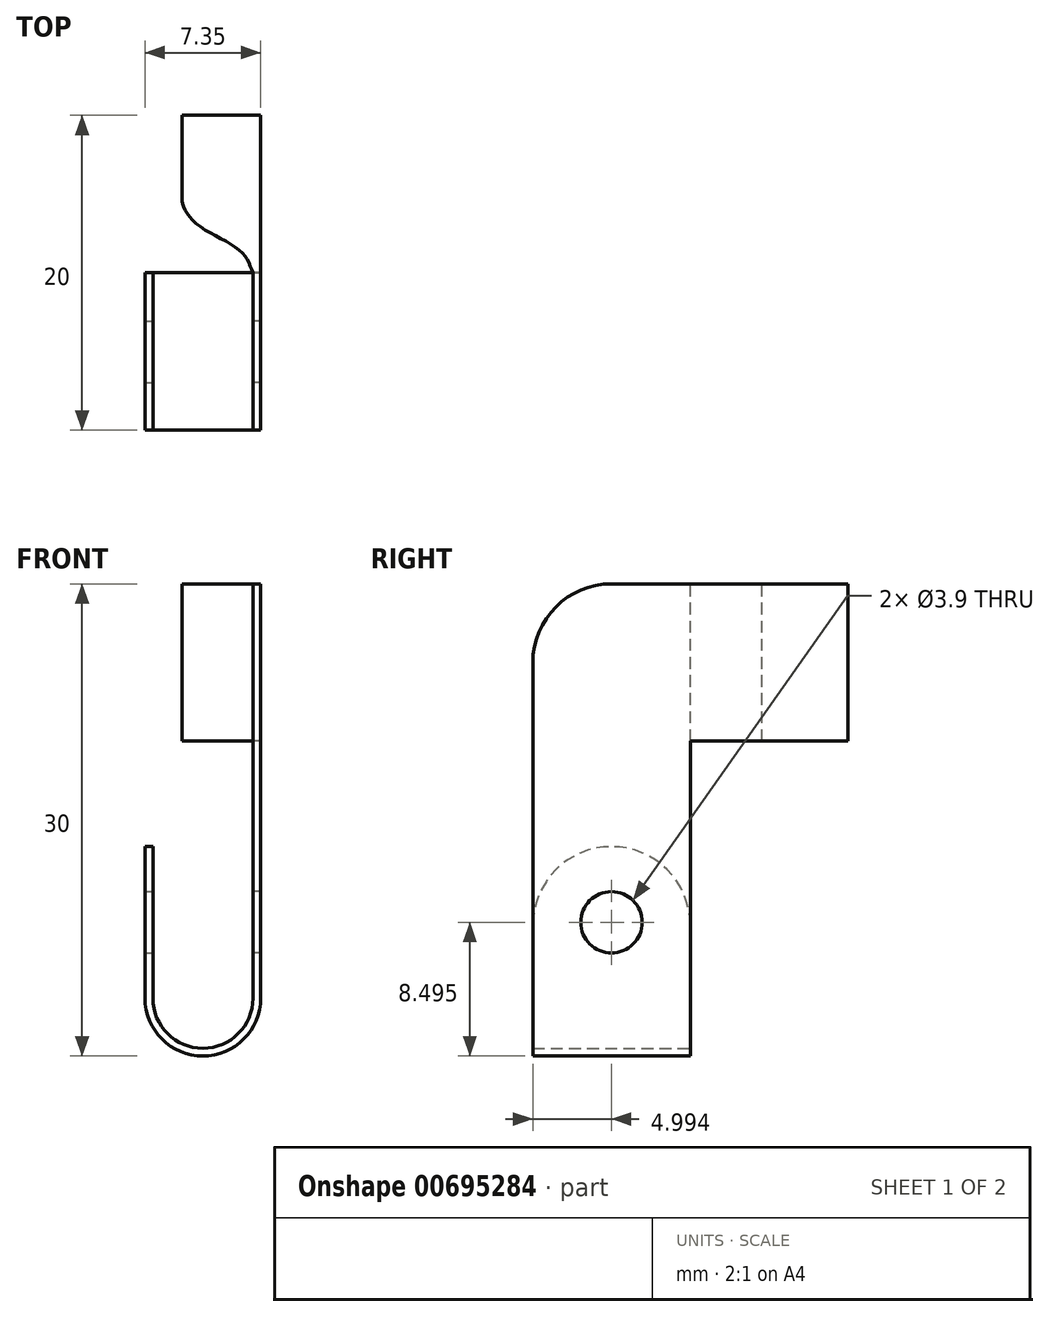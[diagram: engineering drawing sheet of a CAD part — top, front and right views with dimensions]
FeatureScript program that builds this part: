
annotation { "Feature Type Name" : "Feature", "Feature Type Description" : "" }
export const myFeature = defineFeature(function(context is Context, id is Id, definition is map)
    precondition{}
    {
        {
            var Q0;
            Q0=qCreatedBy(makeId("Front.planeOp"),FACE);
            var sketch = newSketch(context, id + "F0", { "sketchPlane" : qUnion([Q0])});
            skLineSegment(sketch, "E0", {"start": v(0, 0) * mm, "end": v(7.44, 0) * mm, "construction": true});
            skLineSegment(sketch, "E1", {"start": v(0, 0) * mm, "end": v(0, 6.37) * mm, "construction": true});
            skArc(sketch, "E2", {"start": v(0, 3.68) * mm, "mid": v(3.67, 0) * mm, "end": v(7.35, 3.67) * mm});
            skArc(sketch, "E3", {"start": v(0.5, 3.68) * mm, "mid": v(3.67, 0.5) * mm, "end": v(6.85, 3.67) * mm});
            skLineSegment(sketch, "E4", {"start": v(0, 3.67) * mm, "end": v(7.35, 3.67) * mm, "construction": true});
            skLineSegment(sketch, "E5", {"start": v(0, 3.68) * mm, "end": v(0, 11.52) * mm});
            skLineSegment(sketch, "E6", {"start": v(0, 15.1) * mm, "end": v(0, 11.52) * mm});
            skLineSegment(sketch, "E7", {"start": v(7.35, 3.67) * mm, "end": v(7.35, 0) * mm, "construction": true});
            skLineSegment(sketch, "E8", {"start": v(6.85, 3.67) * mm, "end": v(6.85, 0) * mm, "construction": true});
            skLineSegment(sketch, "E9", {"start": v(7.35, 3.67) * mm, "end": v(7.35, 20) * mm});
            skLineSegment(sketch, "E10", {"start": v(7.35, 20) * mm, "end": v(6.85, 20) * mm});
            skLineSegment(sketch, "E11", {"start": v(6.85, 20) * mm, "end": v(6.85, 3.67) * mm});
            skLineSegment(sketch, "E12", {"start": v(7.35, 20) * mm, "end": v(7.35, 30) * mm});
            skLineSegment(sketch, "E13.bottom", {"start": v(7.35, 30) * mm, "end": v(6.85, 30) * mm});
            skLineSegment(sketch, "E13.left", {"start": v(7.35, 30) * mm, "end": v(7.35, 20) * mm});
            skLineSegment(sketch, "E13.right", {"start": v(6.85, 30) * mm, "end": v(6.85, 20) * mm});
            skLineSegment(sketch, "E14", {"start": v(6.85, 20) * mm, "end": v(0, 20) * mm, "construction": true});
            skLineSegment(sketch, "E15", {"start": v(0, 3.68) * mm, "end": v(0, 13.3) * mm});
            skLineSegment(sketch, "E16.bottom", {"start": v(0, 13.3) * mm, "end": v(0.5, 13.3) * mm});
            skLineSegment(sketch, "E16.top", {"start": v(0, 3.68) * mm, "end": v(0.5, 3.68) * mm});
            skLineSegment(sketch, "E16.left", {"start": v(0, 13.3) * mm, "end": v(0, 3.68) * mm});
            skLineSegment(sketch, "E16.right", {"start": v(0.5, 13.3) * mm, "end": v(0.5, 3.68) * mm});
            skSolve(sketch);
        }
        {
            var Q0;
            Q0=makeQuery(id+"F0.imprint","IMPRINT",FACE,{"disambiguationData":[TD([[makeQuery(id+"F0.imprint","IMPRINT",EDGE,{"derivedFrom":sQuery(id+"F0.wireOp",EDGE,"E2")}),1.0]])]});
            var Q1;
            Q1=makeQuery(id+"F0.imprint","IMPRINT",FACE,{"disambiguationData":[TD([[makeQuery(id+"F0.imprint","IMPRINT",EDGE,{"derivedFrom":sQuery(id+"F0.wireOp",EDGE,"E16.bottom")}),-1.0]])]});
            extrude(context, id + "F1", {"entities" : qUnion([Q0, Q1]), "depth" : 10 * mm, "offsetDistance" : 25 * mm});
        }
        {
            var Q0;
            Q0=makeQuery(id+"F0.imprint","IMPRINT",FACE,{"disambiguationData":[TD([[makeQuery(id+"F0.imprint","IMPRINT",EDGE,{"derivedFrom":sQuery(id+"F0.wireOp",EDGE,"E13.bottom")}),1.0]])]});
            extrude(context, id + "F2", {"entities" : qUnion([Q0]), "operationType" : NewBodyOperationType.ADD, "depth" : 10 * mm, "offsetDistance" : 25 * mm});
        }
        {
            var Q0;
            Q0=makeQuery(id+"F0.imprint","IMPRINT",FACE,{"disambiguationData":[TD([[makeQuery(id+"F0.imprint","IMPRINT",EDGE,{"derivedFrom":sQuery(id+"F0.wireOp",EDGE,"E13.bottom")}),1.0]])]});
            extrude(context, id + "F3", {"entities" : qUnion([Q0]), "operationType" : NewBodyOperationType.ADD, "oppositeDirection" : true, "depth" : 10 * mm, "offsetDistance" : 25 * mm});
        }
        {
            var Q0;
            {var subQ0=sQuery(id+"F0.wireOp",EDGE,"E13.right");Q0=makeQuery(id+"F3.boolean.opBoolean","MERGE",FACE,{"derivedFrom":[makeQuery(id+"F2.boolean.opBoolean","MERGE",FACE,{"derivedFrom":[makeQuery(id+"F1.opExtrude","SWEPT_FACE",FACE,{"disambiguationData":[OSD([sQuery(id+"F0.wireOp",EDGE,"E11")])]}),makeQuery(id+"F2.opExtrude","SWEPT_FACE",FACE,{"disambiguationData":[OSD([subQ0])]})]}),makeQuery(id+"F3.opExtrude","SWEPT_FACE",FACE,{"disambiguationData":[OSD([subQ0])]})]});}
            var sketch = newSketch(context, id + "F4", { "sketchPlane" : qUnion([Q0])});
            skLineSegment(sketch, "E17", {"start": v(10, 13.3) * mm, "end": v(0, 3.68) * mm, "construction": true});
            skLineSegment(sketch, "E18", {"start": v(0, 3.67) * mm, "end": v(0, 13.33) * mm, "construction": true});
            skLineSegment(sketch, "E19", {"start": v(0, 13.33) * mm, "end": v(10, 3.68) * mm, "construction": true});
            skCircle(sketch, "E20", {"center": v(5, 8.5) * mm, "radius": 1.95 * mm});
            skLineSegment(sketch, "E21", {"start": v(0, 20) * mm, "end": v(0, 30) * mm});
            skSolve(sketch);
        }
        {
            var Q0;
            Q0 = qSketchRegion(id + "F4", true);
            extrude(context, id + "F5", {"entities" : qUnion([Q0]), "operationType" : NewBodyOperationType.REMOVE, "oppositeDirection" : true, "depth" : 25 * mm, "offsetDistance" : 25 * mm});
        }
        {
            var Q0;
            Q0 = qSketchRegion(id + "F4", true);
            extrude(context, id + "F6", {"entities" : qUnion([Q0]), "operationType" : NewBodyOperationType.REMOVE, "depth" : 25 * mm, "offsetDistance" : 25 * mm});
        }
        {
            var Q0;
            Q0=makeQuery(id+"F2.opExtrude","CAP_EDGE",EDGE,{"disambiguationData":[OSD([sQuery(id+"F0.wireOp",EDGE,"E13.bottom")])],"isStart":false});
            var Q1;
            Q1=makeQuery(id+"F1.opExtrude","CAP_EDGE",EDGE,{"disambiguationData":[OSD([sQuery(id+"F0.wireOp",EDGE,"E16.bottom")])],"isStart":false});
            var Q2;
            Q2=makeQuery(id+"F1.opExtrude","CAP_EDGE",EDGE,{"disambiguationData":[OSD([sQuery(id+"F0.wireOp",EDGE,"E16.bottom")])],"isStart":true});
            fillet(context, id + "F7", {"entities" : qUnion([Q0, Q1, Q2]), "radius" : 5 * mm, "tangentPropagation" : true, "allowEdgeOverflow" : false});
        }
        {
            var Q0;
            {var subQ0=sQuery(id+"F4.wireOp",EDGE,"E21");Q0=makeQuery(id+"F4.imprint","IMPRINT",FACE,{"disambiguationData":[TD([[makeQuery(id+"F4.imprint","IMPRINT",EDGE,{"derivedFrom":subQ0}),1.0]])]});}
            extrude(context, id + "F8", {"entities" : qUnion([Q0]), "operationType" : NewBodyOperationType.ADD, "depth" : 4.5 * mm, "offsetDistance" : 25 * mm});
        }
        {
            var Q0;
            {var subQ0=sQuery(id+"F0.wireOp",EDGE,"E13.bottom");Q0=makeQuery(id+"F8.boolean.opBoolean","MERGE",FACE,{"derivedFrom":[makeQuery(id+"F3.boolean.opBoolean","MERGE",FACE,{"derivedFrom":[makeQuery(id+"F2.opExtrude","SWEPT_FACE",FACE,{"disambiguationData":[OSD([subQ0])]}),makeQuery(id+"F3.opExtrude","SWEPT_FACE",FACE,{"disambiguationData":[OSD([subQ0])]})]}),makeQuery(id+"F8.opExtrude","SWEPT_FACE",FACE,{"disambiguationData":[OSD([subQ0,sQuery(id+"F0.wireOp",EDGE,"E13.right")])]})]});}
            var sketch = newSketch(context, id + "F9", { "sketchPlane" : qUnion([Q0])});
            skFitSpline(sketch, "E22", {"points": [v(6.85, 0) * mm, v(6.05, 1.4) * mm, v(3.16, 3.2) * mm, v(2.35, 4.56) * mm, v(2.35, 5) * mm], "startDerivative": vector(-2.26, 5.95) * mm, "endDerivative": vector(0.95, 3.35) * mm});
            skLineSegment(sketch, "E23.bottom", {"start": v(6.85, 0) * mm, "end": v(2.35, 0) * mm});
            skLineSegment(sketch, "E23.top", {"start": v(6.85, 5) * mm, "end": v(2.35, 5) * mm});
            skLineSegment(sketch, "E23.left", {"start": v(6.85, 0) * mm, "end": v(6.85, 5) * mm});
            skLineSegment(sketch, "E23.right", {"start": v(2.35, 0) * mm, "end": v(2.35, 5) * mm});
            skSolve(sketch);
        }
        {
            var Q0;
            {var subQ0=sQuery(id+"F9.wireOp",EDGE,"E23.bottom");Q0=makeQuery(id+"F9.imprint","IMPRINT",FACE,{"disambiguationData":[TD([[makeQuery(id+"F9.imprint","IMPRINT",EDGE,{"derivedFrom":subQ0}),1.0]])]});}
            extrude(context, id + "F10", {"entities" : qUnion([Q0]), "operationType" : NewBodyOperationType.REMOVE, "oppositeDirection" : true, "depth" : 25 * mm, "offsetDistance" : 25 * mm});
        }
    });
